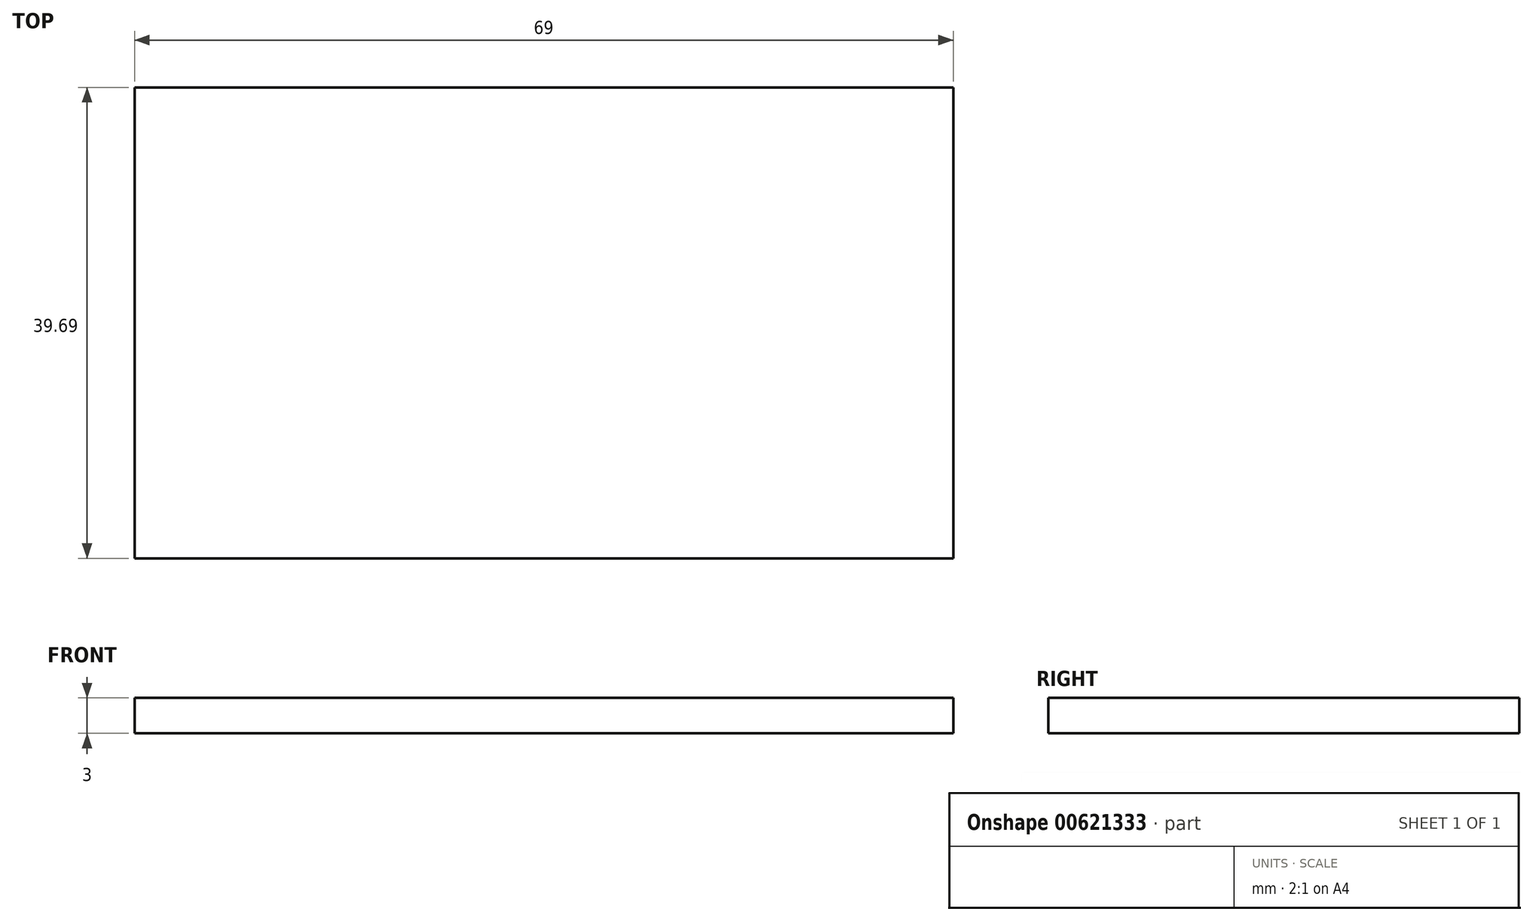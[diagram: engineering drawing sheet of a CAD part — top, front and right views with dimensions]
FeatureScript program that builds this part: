
annotation { "Feature Type Name" : "Feature", "Feature Type Description" : "" }
export const myFeature = defineFeature(function(context is Context, id is Id, definition is map)
    precondition{}
    {
        {
            var Q0;
            Q0=qCreatedBy(makeId("Top.planeOp"),FACE);
            var sketch = newSketch(context, id + "F0", { "sketchPlane" : qUnion([Q0])});
            skLineSegment(sketch, "E0.bottom", {"start": v(-33.86, 0) * mm, "end": v(35.14, 0) * mm});
            skLineSegment(sketch, "E0.top", {"start": v(-33.86, 39.69) * mm, "end": v(35.14, 39.69) * mm});
            skLineSegment(sketch, "E0.left", {"start": v(-33.86, 0) * mm, "end": v(-33.86, 39.69) * mm});
            skLineSegment(sketch, "E0.right", {"start": v(35.14, 0) * mm, "end": v(35.14, 39.69) * mm});
            skSolve(sketch);
        }
        {
            var Q0;
            Q0=makeQuery(id+"F0.imprint","IMPRINT",FACE,{"disambiguationData":[TD([[makeQuery(id+"F0.imprint","IMPRINT",EDGE,{"derivedFrom":sQuery(id+"F0.wireOp",EDGE,"E0.bottom")}),1.0]])]});
            extrude(context, id + "F1", {"entities" : qUnion([Q0]), "depth" : 3 * mm, "offsetDistance" : 25.4 * mm});
        }
    });
